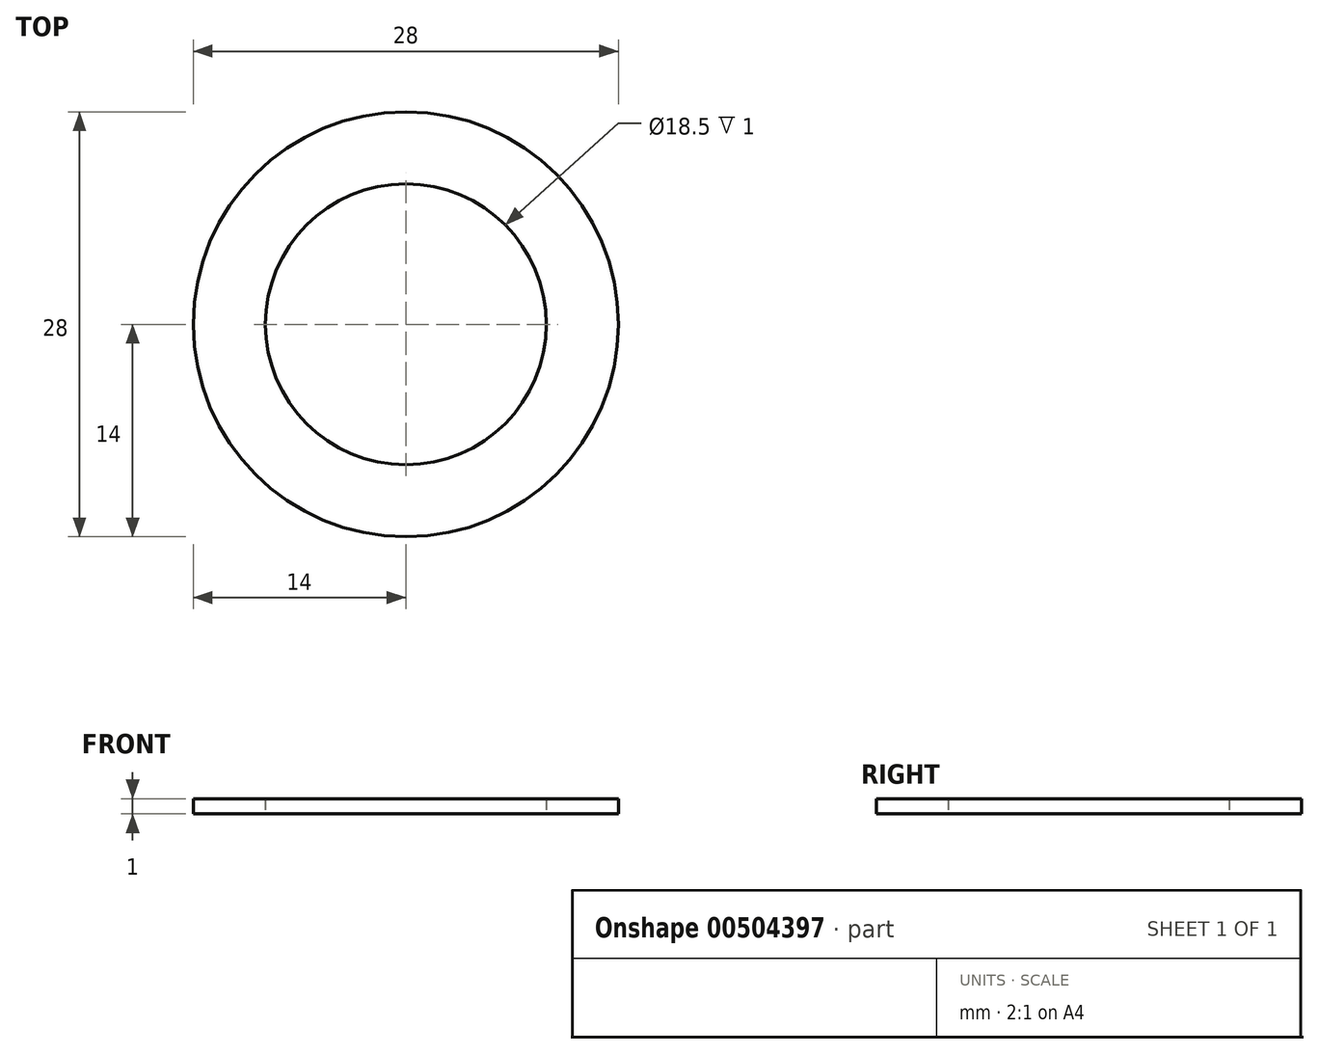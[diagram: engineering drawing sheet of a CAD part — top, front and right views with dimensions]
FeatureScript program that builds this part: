
annotation { "Feature Type Name" : "Feature", "Feature Type Description" : "" }
export const myFeature = defineFeature(function(context is Context, id is Id, definition is map)
    precondition{}
    {
        {
            var Q0;
            Q0=qCreatedBy(makeId("Top.planeOp"),FACE);
            var sketch = newSketch(context, id + "F0", { "sketchPlane" : qUnion([Q0])});
            skCircle(sketch, "E0", {"center": v(0, 0) * mm, "radius": 9.25 * mm});
            skCircle(sketch, "E1", {"center": v(0, 0) * mm, "radius": 14 * mm});
            skSolve(sketch);
        }
        {
            var Q0;
            Q0=makeQuery(id+"F0.imprint","IMPRINT",FACE,{"disambiguationData":[TD([[makeQuery(id+"F0.imprint","IMPRINT",EDGE,{"derivedFrom":sQuery(id+"F0.wireOp",EDGE,"E0")}),-1.0]])]});
            extrude(context, id + "F1", {"entities" : qUnion([Q0]), "depth" : 1 * mm});
        }
    });
